# Revit family: Drinking_Fountain-Bi_Level-Murdock-A172.8-UG-VR_Series
name_source: partatom
category: Plumbing Fixtures
units: mm (PartAtom-declared; Revit-internal decimal feet)

## family parameters
Cut with Voids When Loaded = Yes
Host = Face
OmniClass Number = 23.65.70.14.11
OmniClass Title = Drinking Fountains/Coolers
Part Type = Normal
Room Calculation Point = No
Round Connector Dimension = Use Diameter
Shared = Yes

## types (4) — shared parameters
-LOGO Customer Specified Logo / Graphics = No
-SK5 Cane Detection Skirt for Upper Unit = No
-WF1EZ 1500-Gallon Capacity EZ Door Filter 30-Second Replacement = No
220V 220 Volt/50 Hz or 60 Hz Compressor = No
ADA Compliant = Yes
Activation = Push Button
Assembly Code = D2010800
CW Connection = Yes
CWFU = 1
Cold Water Connection Diameter = 3/8"
Default Elevation = 0"
Description = 14GA Stainless Steel, Vandal-Resistant, Wall-Mounted, Bi-Level Drinking Fountain - In-Unit Refrigeration (8GPH), ADA
Flow Rate = 8.0 GPH
Full Load Amps = 4.1
HW Connection = No
Height From Floor Level = 33"
IAPMO Compliance = ANSI/ASHRAE 18. Unit shall be certified to Public Law 111-380
(NO-LEAD) and NSF/ANSI/CAN 61.
Installation Type = Wall Mounted
Length = 18 1/2"
Manufacturer = Murdock Manufacturing
Product Documentation Link = https://www.murdockmfg.com
Product Page URL = https://www.murdockmfg.com
Rated Watts = 400 W
Shipping Weight = 140 lbs.
URL = https://www.murdockmfg.com
Vent Connection = No
Voltage Nominal = 220 V
WF3 3000-Gallon Capacity, NSF 42+53, 1-Micron Lead Reduction Filter = No
WFU = 1.5
Waste Connection = Yes
Waste Connection Diameter = 1 1/4"
Water Pressure = 20-105 PSIG.
Width = 37 1/8"
cUPC Compliant = Yes
zero-valued in all types: HWFU

## per-type parameters (varying)
| type | F-Flexible Bubbler | F-Stainless Steel Bubbler | Finish | Finish- Push Button | Finish-Bubbler | Material | Waste Connection Height |
| A172108F-UG-VR | Yes | No | Stainless Steel-Murdock-Gray | Stainless Steel-Murdock-Gray | Murdock- White | Stainless Steel-Murdock-Gray | 22 1/8" |
| A172408F-UG-VR | Yes | No | Stainless Steel-Murdock-Brushed Satin | Stainless Steel-Murdock-Brushed Satin | Murdock- White | Stainless Steel-Murdock-Brushed Satin | 22 1/4" |
| A172108S-UG-VR | No | Yes | Stainless Steel-Murdock-Gray | Stainless Steel-Murdock-Gray | Stainless Steel-Murdock-Gray | Stainless Steel-Murdock-Gray | 22 1/4" |
| A172408S-UG-VR | No | Yes | Stainless Steel-Murdock-Brushed Satin | Stainless Steel-Murdock-Brushed Satin | Stainless Steel-Murdock-Brushed Satin | Stainless Steel-Murdock-Brushed Satin | 22 1/4" |

note: column(s) folded — value = type name in every type: Model

## geometry (parser evidence)
native form markers: Sweep x3
no freeform markers — native parametric forms only
